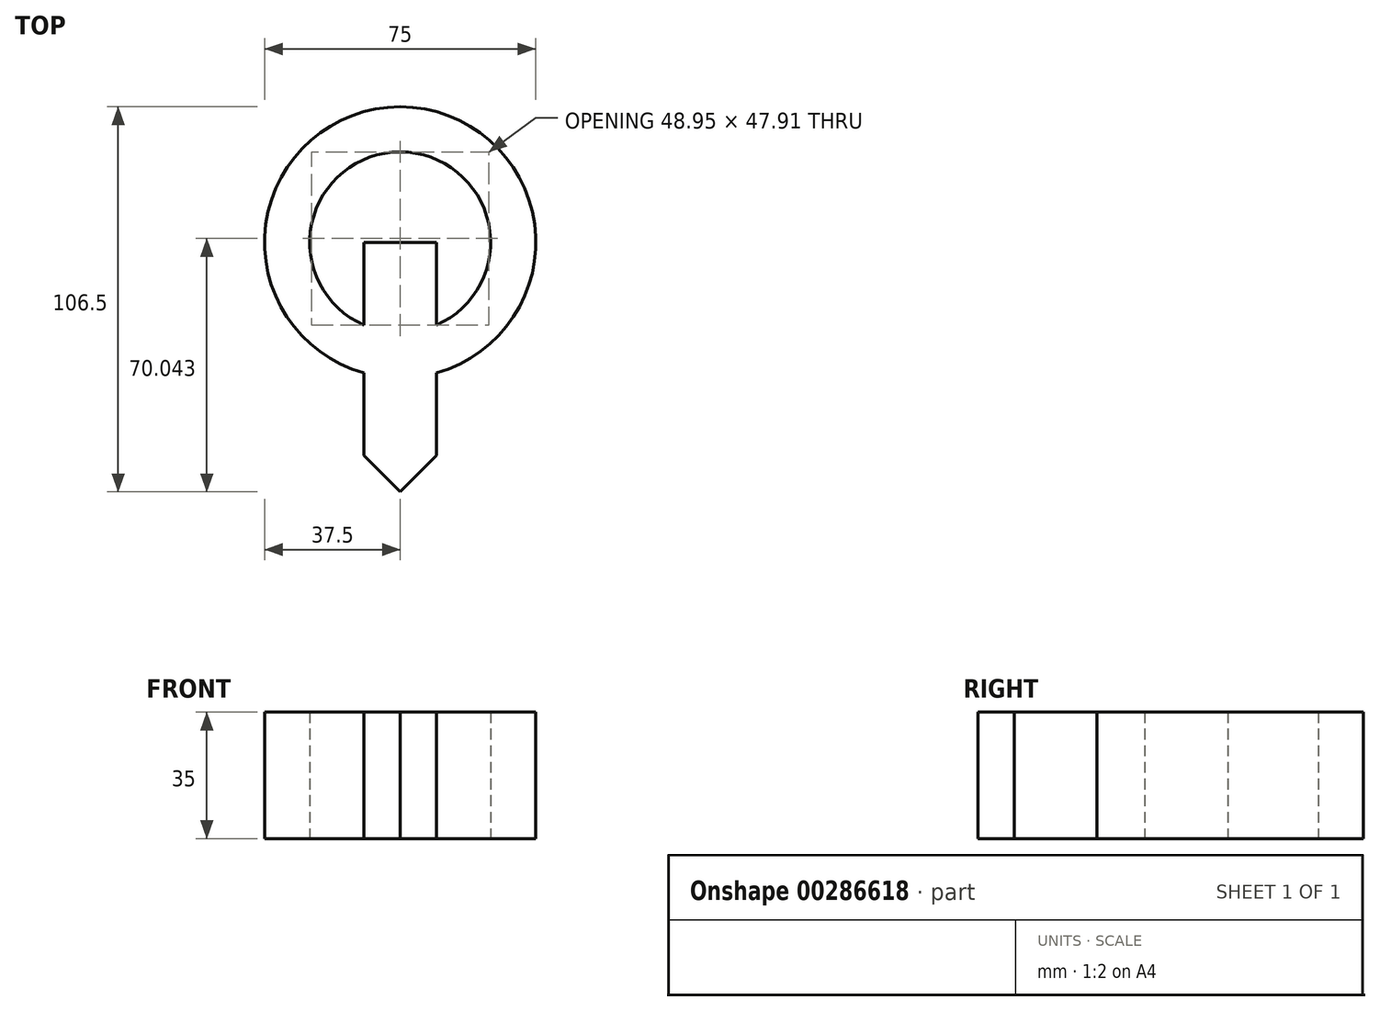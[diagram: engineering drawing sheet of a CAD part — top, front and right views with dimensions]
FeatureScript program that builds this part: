
annotation { "Feature Type Name" : "Feature", "Feature Type Description" : "" }
export const myFeature = defineFeature(function(context is Context, id is Id, definition is map)
    precondition{}
    {
        {
            var Q0;
            Q0=qCreatedBy(makeId("Top.planeOp"),FACE);
            var sketch = newSketch(context, id + "F0", { "sketchPlane" : qUnion([Q0])});
            skCircle(sketch, "E0", {"center": v(0, 0) * mm, "radius": 25 * mm});
            skCircle(sketch, "E1", {"center": v(0, 0) * mm, "radius": 37.5 * mm});
            skSolve(sketch);
        }
        {
            var Q0;
            Q0=makeQuery(id+"F0.imprint","IMPRINT",FACE,{"disambiguationData":[TD([[makeQuery(id+"F0.imprint","IMPRINT",EDGE,{"derivedFrom":sQuery(id+"F0.wireOp",EDGE,"E0")}),-1.0]])]});
            extrude(context, id + "F1", {"entities" : qUnion([Q0]), "depth" : 35 * mm});
        }
        {
            var Q0;
            Q0=qCreatedBy(makeId("Front.planeOp"),FACE);
            var sketch = newSketch(context, id + "F2", { "sketchPlane" : qUnion([Q0])});
            skLineSegment(sketch, "E2.bottom", {"start": v(-10, 35) * mm, "end": v(10, 35) * mm});
            skLineSegment(sketch, "E2.top", {"start": v(-10, 0) * mm, "end": v(10, 0) * mm});
            skLineSegment(sketch, "E2.left", {"start": v(-10, 35) * mm, "end": v(-10, 0) * mm});
            skLineSegment(sketch, "E2.right", {"start": v(10, 35) * mm, "end": v(10, 0) * mm});
            skSolve(sketch);
        }
        {
            var Q0;
            Q0 = qSketchRegion(id + "F2", true);
            extrude(context, id + "F3", {"entities" : qUnion([Q0]), "operationType" : NewBodyOperationType.ADD, "depth" : 69 * mm});
        }
        {
            var Q0;
            Q0=makeQuery(id+"F3.opExtrude","CAP_EDGE",EDGE,{"disambiguationData":[OSD([sQuery(id+"F2.wireOp",EDGE,"E2.left")])],"isStart":false});
            var Q1;
            Q1=makeQuery(id+"F3.opExtrude","CAP_EDGE",EDGE,{"disambiguationData":[OSD([sQuery(id+"F2.wireOp",EDGE,"E2.right")])],"isStart":false});
            chamfer(context, id + "F4", {"entities" : qUnion([Q0, Q1]), "width" : 10 * mm, "tangentPropagation" : true});
        }
    });
